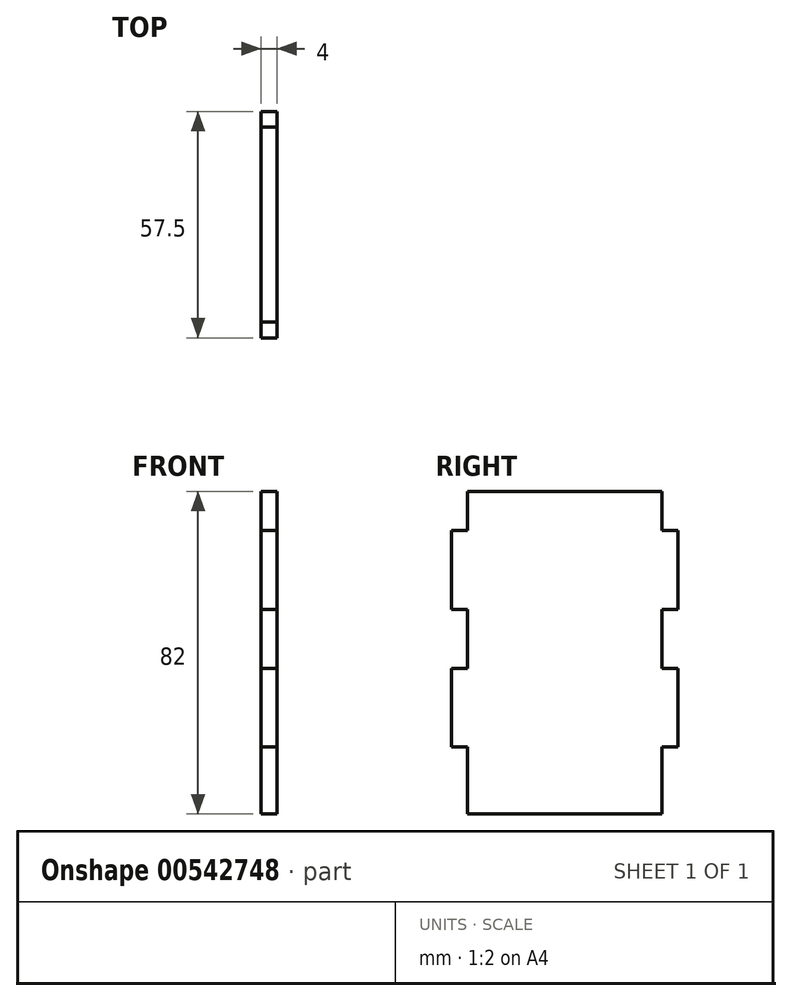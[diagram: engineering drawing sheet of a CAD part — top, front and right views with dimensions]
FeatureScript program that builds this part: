
annotation { "Feature Type Name" : "Feature", "Feature Type Description" : "" }
export const myFeature = defineFeature(function(context is Context, id is Id, definition is map)
    precondition{}
    {
        {
            var Q0;
            Q0=qCreatedBy(makeId("Right.planeOp"),FACE);
            var sketch = newSketch(context, id + "F0", { "sketchPlane" : qUnion([Q0])});
            skLineSegment(sketch, "E0.top", {"start": v(-25.5, -34.8) * mm, "end": v(24, -34.8) * mm});
            skLineSegment(sketch, "E0.left", {"start": v(-25.5, 47.2) * mm, "end": v(-25.5, 37.2) * mm});
            skLineSegment(sketch, "E0.right", {"start": v(24, 47.2) * mm, "end": v(24, 37.2) * mm});
            skLineSegment(sketch, "E1.bottom", {"start": v(-25.5, 37.2) * mm, "end": v(-29.5, 37.2) * mm});
            skLineSegment(sketch, "E1.top", {"start": v(-25.5, 17.2) * mm, "end": v(-29.5, 17.2) * mm});
            skLineSegment(sketch, "E1.right", {"start": v(-29.5, 37.2) * mm, "end": v(-29.5, 17.2) * mm});
            skLineSegment(sketch, "E2.bottom", {"start": v(-25.5, 2.2) * mm, "end": v(-29.5, 2.2) * mm});
            skLineSegment(sketch, "E2.top", {"start": v(-25.5, -17.8) * mm, "end": v(-29.5, -17.8) * mm});
            skLineSegment(sketch, "E2.right", {"start": v(-29.5, 2.2) * mm, "end": v(-29.5, -17.8) * mm});
            skLineSegment(sketch, "E3.bottom", {"start": v(24, 37.2) * mm, "end": v(28, 37.2) * mm});
            skLineSegment(sketch, "E3.top", {"start": v(24, 17.2) * mm, "end": v(28, 17.2) * mm});
            skLineSegment(sketch, "E3.right", {"start": v(28, 37.2) * mm, "end": v(28, 17.2) * mm});
            skLineSegment(sketch, "E4.bottom", {"start": v(24, 2.2) * mm, "end": v(28, 2.2) * mm});
            skLineSegment(sketch, "E4.top", {"start": v(24, -17.8) * mm, "end": v(28, -17.8) * mm});
            skLineSegment(sketch, "E4.right", {"start": v(28, 2.2) * mm, "end": v(28, -17.8) * mm});
            skLineSegment(sketch, "E5.trimOffspring", {"start": v(-25.5, 17.2) * mm, "end": v(-25.5, 2.2) * mm});
            skLineSegment(sketch, "E6.trimOffspring", {"start": v(-25.5, -17.8) * mm, "end": v(-25.5, -34.8) * mm});
            skLineSegment(sketch, "E7.trimOffspring", {"start": v(24, -17.8) * mm, "end": v(24, -34.8) * mm});
            skLineSegment(sketch, "E8", {"start": v(24, 17.2) * mm, "end": v(24, 2.2) * mm});
            skLineSegment(sketch, "E9", {"start": v(-25.5, 47.2) * mm, "end": v(24, 47.2) * mm});
            skSolve(sketch);
        }
        {
            var Q0;
            Q0=makeQuery(id+"F0.imprint","IMPRINT",FACE,{"disambiguationData":[TD([[makeQuery(id+"F0.imprint","IMPRINT",EDGE,{"derivedFrom":sQuery(id+"F0.wireOp",EDGE,"E0.top")}),1.0]])]});
            extrude(context, id + "F1", {"entities" : qUnion([Q0]), "depth" : 4 * mm, "offsetDistance" : 25 * mm});
        }
    });
